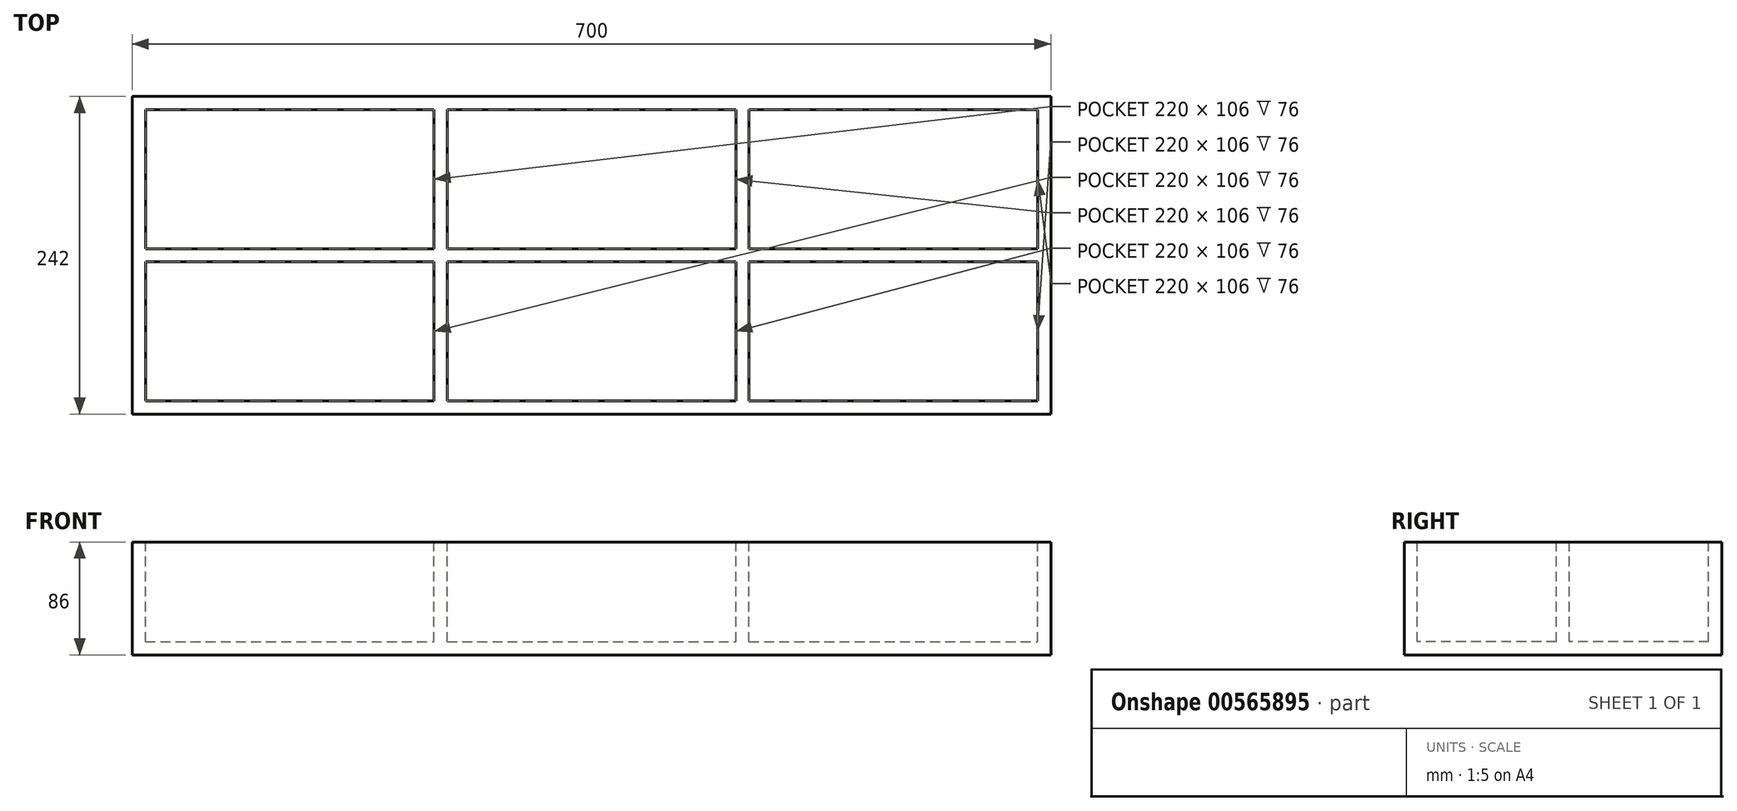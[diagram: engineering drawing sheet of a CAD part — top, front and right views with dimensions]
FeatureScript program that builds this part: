
annotation { "Feature Type Name" : "Feature", "Feature Type Description" : "" }
export const myFeature = defineFeature(function(context is Context, id is Id, definition is map)
    precondition{}
    {
        {
            assignVariable(context, id + "F0", {"name" : "thickness", "anyValue" : 10});
        }
        {
            assignVariable(context, id + "F1", {"name" : "height", "anyValue" : 86});
        }
        {
            var Q0;
            Q0=qCreatedBy(makeId("Top.planeOp"),FACE);
            var sketch = newSketch(context, id + "F2", { "sketchPlane" : qUnion([Q0])});
            skLineSegment(sketch, "E0.bottom", {"start": v(-260.53, 118.7) * mm, "end": v(-40.53, 118.7) * mm});
            skLineSegment(sketch, "E0.top", {"start": v(-260.53, 12.7) * mm, "end": v(-40.53, 12.7) * mm});
            skLineSegment(sketch, "E0.left", {"start": v(-260.53, 118.7) * mm, "end": v(-260.53, 12.7) * mm});
            skLineSegment(sketch, "E0.right", {"start": v(-40.53, 118.7) * mm, "end": v(-40.53, 12.7) * mm});
            skLineSegment(sketch, "E1.bottom", {"start": v(-30.53, 118.7) * mm, "end": v(189.47, 118.7) * mm});
            skLineSegment(sketch, "E1.top", {"start": v(-30.53, 12.7) * mm, "end": v(189.47, 12.7) * mm});
            skLineSegment(sketch, "E1.left", {"start": v(-30.53, 118.7) * mm, "end": v(-30.53, 12.7) * mm});
            skLineSegment(sketch, "E1.right", {"start": v(189.47, 118.7) * mm, "end": v(189.47, 12.7) * mm});
            skLineSegment(sketch, "E2.bottom", {"start": v(199.47, 118.7) * mm, "end": v(419.47, 118.7) * mm});
            skLineSegment(sketch, "E2.top", {"start": v(199.47, 12.7) * mm, "end": v(419.47, 12.7) * mm});
            skLineSegment(sketch, "E2.left", {"start": v(199.47, 118.7) * mm, "end": v(199.47, 12.7) * mm});
            skLineSegment(sketch, "E2.right", {"start": v(419.47, 118.7) * mm, "end": v(419.47, 12.7) * mm});
            skLineSegment(sketch, "E3.bottom", {"start": v(-260.53, 2.7) * mm, "end": v(-40.53, 2.7) * mm});
            skLineSegment(sketch, "E3.top", {"start": v(-260.53, -103.3) * mm, "end": v(-40.53, -103.3) * mm});
            skLineSegment(sketch, "E3.left", {"start": v(-260.53, 2.7) * mm, "end": v(-260.53, -103.3) * mm});
            skLineSegment(sketch, "E3.right", {"start": v(-40.53, 2.7) * mm, "end": v(-40.53, -103.3) * mm});
            skLineSegment(sketch, "E4.bottom", {"start": v(-30.53, 2.7) * mm, "end": v(189.47, 2.7) * mm});
            skLineSegment(sketch, "E4.top", {"start": v(-30.53, -103.3) * mm, "end": v(189.47, -103.3) * mm});
            skLineSegment(sketch, "E4.left", {"start": v(-30.53, 2.7) * mm, "end": v(-30.53, -103.3) * mm});
            skLineSegment(sketch, "E4.right", {"start": v(189.47, 2.7) * mm, "end": v(189.47, -103.3) * mm});
            skLineSegment(sketch, "E5.bottom", {"start": v(199.47, 2.7) * mm, "end": v(419.47, 2.7) * mm});
            skLineSegment(sketch, "E5.top", {"start": v(199.47, -103.3) * mm, "end": v(419.47, -103.3) * mm});
            skLineSegment(sketch, "E5.left", {"start": v(199.47, 2.7) * mm, "end": v(199.47, -103.3) * mm});
            skLineSegment(sketch, "E5.right", {"start": v(419.47, 2.7) * mm, "end": v(419.47, -103.3) * mm});
            skLineSegment(sketch, "E6.bottom", {"start": v(-270.53, 128.7) * mm, "end": v(429.47, 128.7) * mm});
            skLineSegment(sketch, "E6.top", {"start": v(-270.53, -113.3) * mm, "end": v(429.47, -113.3) * mm});
            skLineSegment(sketch, "E6.left", {"start": v(-270.53, 128.7) * mm, "end": v(-270.53, -113.3) * mm});
            skLineSegment(sketch, "E6.right", {"start": v(429.47, 128.7) * mm, "end": v(429.47, -113.3) * mm});
            skLineSegment(sketch, "E7", {"start": v(-40.53, 118.7) * mm, "end": v(-30.53, 118.7) * mm, "construction": true});
            skLineSegment(sketch, "E8", {"start": v(189.47, 118.7) * mm, "end": v(199.47, 118.7) * mm, "construction": true});
            skLineSegment(sketch, "E9", {"start": v(-40.53, -103.3) * mm, "end": v(-30.53, -103.3) * mm, "construction": true});
            skLineSegment(sketch, "E10", {"start": v(189.47, -103.3) * mm, "end": v(199.47, -103.3) * mm, "construction": true});
            skLineSegment(sketch, "E11", {"start": v(-260.53, 12.7) * mm, "end": v(-260.53, 2.7) * mm, "construction": true});
            skLineSegment(sketch, "E12", {"start": v(-30.53, 12.7) * mm, "end": v(-30.53, 2.7) * mm, "construction": true});
            skLineSegment(sketch, "E13", {"start": v(199.47, 12.7) * mm, "end": v(199.47, 2.7) * mm, "construction": true});
            skLineSegment(sketch, "E14", {"start": v(-260.53, 118.7) * mm, "end": v(-270.53, 118.7) * mm, "construction": true});
            skLineSegment(sketch, "E15", {"start": v(-260.53, 118.7) * mm, "end": v(-260.53, 128.7) * mm, "construction": true});
            skLineSegment(sketch, "E16", {"start": v(-260.53, -103.3) * mm, "end": v(-260.53, -113.3) * mm, "construction": true});
            skLineSegment(sketch, "E17", {"start": v(-260.53, -103.3) * mm, "end": v(-270.53, -103.3) * mm, "construction": true});
            skLineSegment(sketch, "E18", {"start": v(419.47, 118.7) * mm, "end": v(429.47, 118.7) * mm, "construction": true});
            skLineSegment(sketch, "E19", {"start": v(419.47, 12.7) * mm, "end": v(419.47, 2.7) * mm, "construction": true});
            skLineSegment(sketch, "E20", {"start": v(419.47, -103.3) * mm, "end": v(429.47, -103.3) * mm, "construction": true});
            skLineSegment(sketch, "E21", {"start": v(-150.53, 118.7) * mm, "end": v(-150.53, 12.7) * mm, "construction": true});
            skLineSegment(sketch, "E22", {"start": v(-260.53, 65.7) * mm, "end": v(-40.53, 65.7) * mm, "construction": true});
            skLineSegment(sketch, "E23", {"start": v(-260.53, -50.3) * mm, "end": v(-40.53, -50.3) * mm, "construction": true});
            skLineSegment(sketch, "E24", {"start": v(-150.53, 2.7) * mm, "end": v(-150.53, -103.3) * mm, "construction": true});
            skLineSegment(sketch, "E25", {"start": v(79.47, 118.7) * mm, "end": v(79.47, 12.7) * mm, "construction": true});
            skLineSegment(sketch, "E26", {"start": v(79.47, 2.7) * mm, "end": v(79.47, -103.3) * mm, "construction": true});
            skLineSegment(sketch, "E27", {"start": v(-30.53, 65.7) * mm, "end": v(189.47, 65.7) * mm, "construction": true});
            skLineSegment(sketch, "E28", {"start": v(-30.53, -50.3) * mm, "end": v(189.47, -50.3) * mm, "construction": true});
            skLineSegment(sketch, "E29", {"start": v(202.48, 65.7) * mm, "end": v(419.47, 65.7) * mm, "construction": true});
            skPoint(sketch, "E29.startSnap0", {"position": v(199.47, 65.7) * mm});
            skLineSegment(sketch, "E30", {"start": v(309.47, 118.7) * mm, "end": v(309.47, 12.7) * mm, "construction": true});
            skLineSegment(sketch, "E31", {"start": v(199.47, -50.3) * mm, "end": v(419.47, -50.3) * mm, "construction": true});
            skLineSegment(sketch, "E32", {"start": v(309.47, 2.7) * mm, "end": v(309.47, -103.3) * mm, "construction": true});
            skSolve(sketch);
        }
        {
            var Q0;
            Q0=makeQuery(id+"F2.imprint","IMPRINT",FACE,{"disambiguationData":[TD([[makeQuery(id+"F2.imprint","IMPRINT",EDGE,{"derivedFrom":sQuery(id+"F2.wireOp",EDGE,"E0.bottom")}),1.0]])]});
            var Q1;
            Q1=makeQuery(id+"F2.imprint","IMPRINT",FACE,{"disambiguationData":[TD([[makeQuery(id+"F2.imprint","IMPRINT",EDGE,{"derivedFrom":sQuery(id+"F2.wireOp",EDGE,"E0.bottom")}),-1.0]])]});
            var Q2;
            Q2=makeQuery(id+"F2.imprint","IMPRINT",FACE,{"disambiguationData":[TD([[makeQuery(id+"F2.imprint","IMPRINT",EDGE,{"derivedFrom":sQuery(id+"F2.wireOp",EDGE,"E3.bottom")}),-1.0]])]});
            var Q3;
            Q3=makeQuery(id+"F2.imprint","IMPRINT",FACE,{"disambiguationData":[TD([[makeQuery(id+"F2.imprint","IMPRINT",EDGE,{"derivedFrom":sQuery(id+"F2.wireOp",EDGE,"E4.bottom")}),-1.0]])]});
            var Q4;
            Q4=makeQuery(id+"F2.imprint","IMPRINT",FACE,{"disambiguationData":[TD([[makeQuery(id+"F2.imprint","IMPRINT",EDGE,{"derivedFrom":sQuery(id+"F2.wireOp",EDGE,"E1.bottom")}),-1.0]])]});
            var Q5;
            Q5=makeQuery(id+"F2.imprint","IMPRINT",FACE,{"disambiguationData":[TD([[makeQuery(id+"F2.imprint","IMPRINT",EDGE,{"derivedFrom":sQuery(id+"F2.wireOp",EDGE,"E2.bottom")}),-1.0]])]});
            var Q6;
            Q6=makeQuery(id+"F2.imprint","IMPRINT",FACE,{"disambiguationData":[TD([[makeQuery(id+"F2.imprint","IMPRINT",EDGE,{"derivedFrom":sQuery(id+"F2.wireOp",EDGE,"E5.bottom")}),-1.0]])]});
            extrude(context, id + "F3", {"entities" : qUnion([Q0, Q1, Q2, Q3, Q4, Q5, Q6]), "oppositeDirection" : true, "depth" : (getVariable(context, 'height')) * mm, "offsetDistance" : 25 * mm});
        }
        {
            var Q0;
            Q0=makeQuery(id+"F2.imprint","IMPRINT",FACE,{"disambiguationData":[TD([[makeQuery(id+"F2.imprint","IMPRINT",EDGE,{"derivedFrom":sQuery(id+"F2.wireOp",EDGE,"E0.bottom")}),-1.0]])]});
            var Q1;
            Q1=makeQuery(id+"F2.imprint","IMPRINT",FACE,{"disambiguationData":[TD([[makeQuery(id+"F2.imprint","IMPRINT",EDGE,{"derivedFrom":sQuery(id+"F2.wireOp",EDGE,"E3.bottom")}),-1.0]])]});
            var Q2;
            Q2=makeQuery(id+"F2.imprint","IMPRINT",FACE,{"disambiguationData":[TD([[makeQuery(id+"F2.imprint","IMPRINT",EDGE,{"derivedFrom":sQuery(id+"F2.wireOp",EDGE,"E1.bottom")}),-1.0]])]});
            var Q3;
            Q3=makeQuery(id+"F2.imprint","IMPRINT",FACE,{"disambiguationData":[TD([[makeQuery(id+"F2.imprint","IMPRINT",EDGE,{"derivedFrom":sQuery(id+"F2.wireOp",EDGE,"E4.bottom")}),-1.0]])]});
            var Q4;
            Q4=makeQuery(id+"F2.imprint","IMPRINT",FACE,{"disambiguationData":[TD([[makeQuery(id+"F2.imprint","IMPRINT",EDGE,{"derivedFrom":sQuery(id+"F2.wireOp",EDGE,"E2.bottom")}),-1.0]])]});
            var Q5;
            Q5=makeQuery(id+"F2.imprint","IMPRINT",FACE,{"disambiguationData":[TD([[makeQuery(id+"F2.imprint","IMPRINT",EDGE,{"derivedFrom":sQuery(id+"F2.wireOp",EDGE,"E5.bottom")}),-1.0]])]});
            extrude(context, id + "F4", {"entities" : qUnion([Q0, Q1, Q2, Q3, Q4, Q5]), "operationType" : NewBodyOperationType.REMOVE, "oppositeDirection" : true, "depth" : (getVariable(context, 'height') - getVariable(context, 'thickness')) * mm, "offsetDistance" : 25 * mm});
        }
    });
